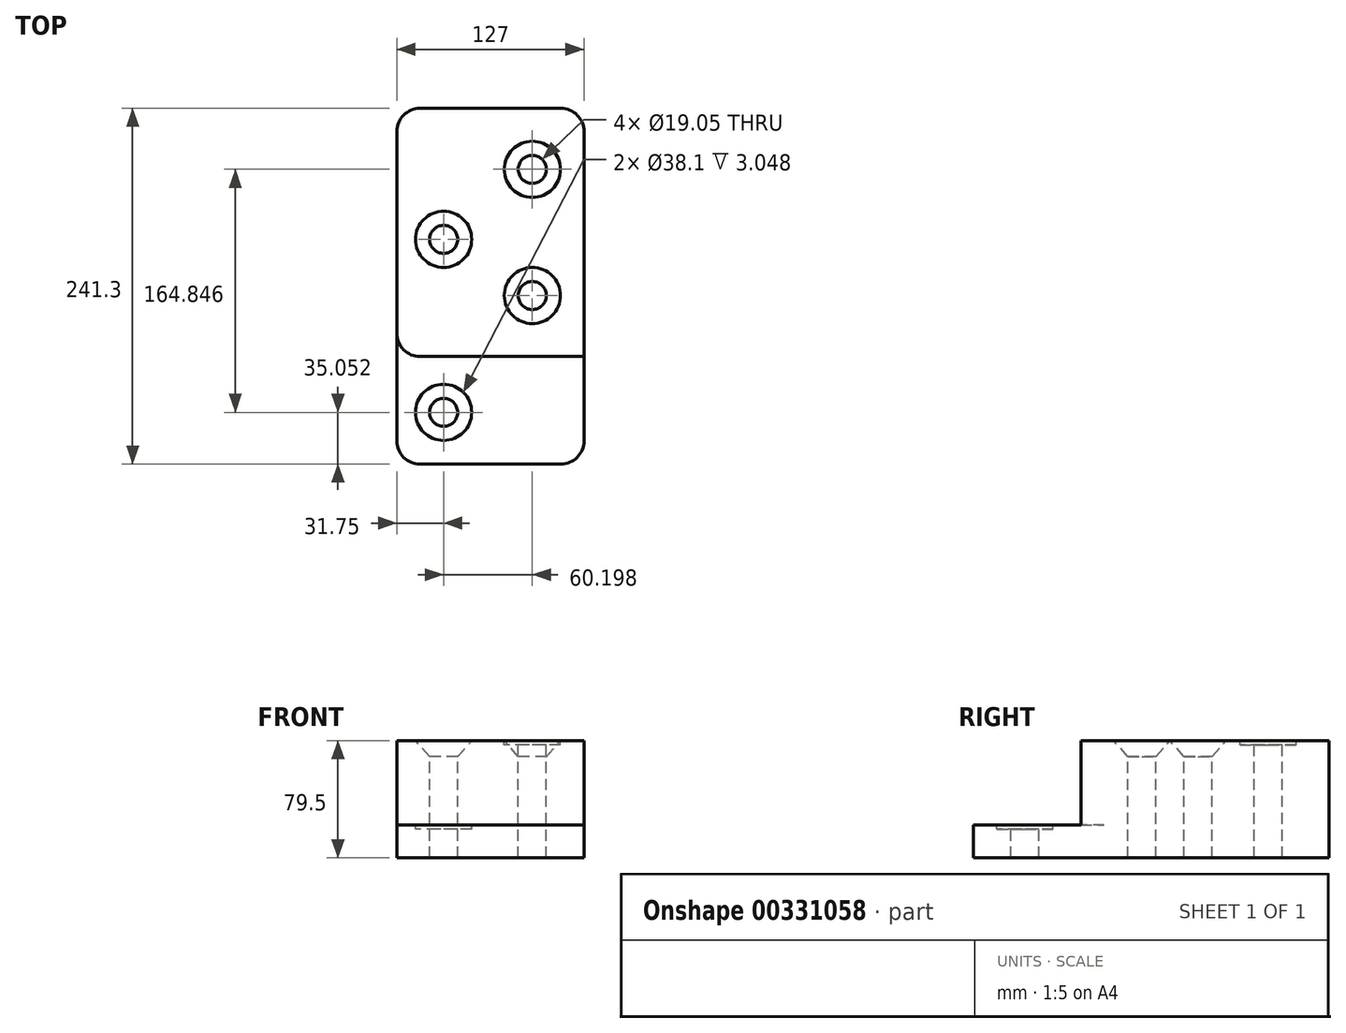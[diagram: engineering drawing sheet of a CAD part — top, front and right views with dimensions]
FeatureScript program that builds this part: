
annotation { "Feature Type Name" : "Feature", "Feature Type Description" : "" }
export const myFeature = defineFeature(function(context is Context, id is Id, definition is map)
    precondition{}
    {
        {
            var Q0;
            Q0=qCreatedBy(makeId("Front.planeOp"),FACE);
            var sketch = newSketch(context, id + "F0", { "sketchPlane" : qUnion([Q0])});
            skLineSegment(sketch, "E0", {"start": v(-63.5, 0) * mm, "end": v(63.5, 0) * mm});
            skLineSegment(sketch, "E1", {"start": v(63.5, 0) * mm, "end": v(63.5, 79.5) * mm});
            skLineSegment(sketch, "E2", {"start": v(63.5, 79.5) * mm, "end": v(-63.5, 79.5) * mm});
            skLineSegment(sketch, "E3", {"start": v(-63.5, 79.5) * mm, "end": v(-63.5, 0) * mm});
            skSolve(sketch);
        }
        {
            var Q0;
            Q0 = qSketchRegion(id + "F0", true);
            extrude(context, id + "F1", {"entities" : qUnion([Q0]), "oppositeDirection" : true, "depth" : 241.3 * mm});
        }
        {
            var Q0;
            Q0=makeQuery(id+"F1.opExtrude","SWEPT_FACE",FACE,{"disambiguationData":[OSD([sQuery(id+"F0.wireOp",EDGE,"E1")])]});
            var sketch = newSketch(context, id + "F2", { "sketchPlane" : qUnion([Q0])});
            skLineSegment(sketch, "E4.0", {"start": v(72.9, 79.5) * mm, "end": v(0, 79.5) * mm});
            skLineSegment(sketch, "E5.0", {"start": v(0, 22.35) * mm, "end": v(0, 79.5) * mm});
            skLineSegment(sketch, "E6", {"start": v(0, 22.35) * mm, "end": v(72.9, 22.35) * mm});
            skLineSegment(sketch, "E7", {"start": v(72.9, 22.35) * mm, "end": v(72.9, 79.5) * mm});
            skPoint(sketch, "E8.orphan", {"position": v(241.3, 79.5) * mm});
            skPoint(sketch, "E9.orphan", {"position": v(0, 0) * mm});
            skLineSegment(sketch, "E10.0", {"start": v(241.3, 0) * mm, "end": v(0, 0) * mm});
            skSolve(sketch);
        }
        {
            var Q0;
            Q0 = qSketchRegion(id + "F2", true);
            extrude(context, id + "F3", {"entities" : qUnion([Q0]), "operationType" : NewBodyOperationType.REMOVE, "endBound" : BoundingType.THROUGH_ALL, "oppositeDirection" : true, "depth" : 25.4 * mm});
        }
        {
            var Q0;
            Q0=makeQuery(id+"F3.boolean.opBoolean","COPY",FACE,{"derivedFrom":makeQuery(id+"F3.opExtrude","SWEPT_FACE",FACE,{"disambiguationData":[OSD([sQuery(id+"F2.wireOp",EDGE,"E6")])]})});
            var sketch = newSketch(context, id + "F4", { "sketchPlane" : qUnion([Q0])});
            skPoint(sketch, "E11", {"position": v(-31.75, 35.05) * mm});
            skLineSegment(sketch, "E12.0", {"start": v(63.5, 0) * mm, "end": v(63.5, 72.9) * mm});
            skLineSegment(sketch, "E13.0", {"start": v(-63.5, 0) * mm, "end": v(63.5, 0) * mm});
            skPoint(sketch, "E14", {"position": v(28.45, 199.9) * mm});
            skLineSegment(sketch, "E15.0", {"start": v(63.5, 241.3) * mm, "end": v(63.5, 72.9) * mm});
            skLineSegment(sketch, "E16.0", {"start": v(63.5, 241.3) * mm, "end": v(-63.5, 241.3) * mm});
            skLineSegment(sketch, "E17.0", {"start": v(-63.5, 72.9) * mm, "end": v(63.5, 72.9) * mm});
            skSolve(sketch);
        }
        {
            var Q0;
            Q0=makeQuery(id+"F1.opExtrude","SWEPT_FACE",FACE,{"disambiguationData":[OSD([sQuery(id+"F0.wireOp",EDGE,"E2")])]});
            var sketch = newSketch(context, id + "F5", { "sketchPlane" : qUnion([Q0])});
            skPoint(sketch, "E18", {"position": v(-31.75, 152.4) * mm});
            skPoint(sketch, "E19", {"position": v(28.45, 206.25) * mm});
            skPoint(sketch, "E20", {"position": v(28.45, 114.3) * mm});
            skLineSegment(sketch, "E21.0", {"start": v(-63.5, 241.3) * mm, "end": v(-63.5, 72.9) * mm});
            skPoint(sketch, "E22.0", {"position": v(0, 72.9) * mm});
            skLineSegment(sketch, "E23.0", {"start": v(-63.5, 72.9) * mm, "end": v(63.5, 72.9) * mm});
            skLineSegment(sketch, "E24.0.0", {"start": v(63.5, 72.9) * mm, "end": v(63.5, 0) * mm});
            skLineSegment(sketch, "E24.0.2", {"start": v(63.5, 72.9) * mm, "end": v(63.5, 241.3) * mm});
            skLineSegment(sketch, "E24.0.4", {"start": v(63.5, 241.3) * mm, "end": v(63.5, 72.9) * mm});
            skLineSegment(sketch, "E25.0", {"start": v(63.5, 241.3) * mm, "end": v(-63.5, 241.3) * mm});
            skPoint(sketch, "E26.orphan", {"position": v(63.5, 0) * mm});
            skSolve(sketch);
        }
        {
            var Q0;
            Q0=sQuery(id+"F5.wireOp",VERTEX,"E18");
            var Q1;
            Q1=sQuery(id+"F5.wireOp",VERTEX,"E20");
            var Q2;
            Q2=makeQuery(id+"F1.opExtrude","SWEPT_BODY",BODY,{"disambiguationData":[OSD([sQuery(id+"F0.wireOp",EDGE,"E0"),sQuery(id+"F0.wireOp",EDGE,"E1"),sQuery(id+"F0.wireOp",EDGE,"E2"),sQuery(id+"F0.wireOp",EDGE,"E3")])]});
            hole(context, id + "F6", {"style" : HoleStyle.C_SINK, "endStyle" : HoleEndStyle.THROUGH, "holeDiameter" : 19.05 * mm, "cSinkDiameter" : 38.1 * mm, "cSinkAngle" : 82 * degree, "tappedDepth" : 12.7 * mm, "tapClearance" : 3, "locations" : qUnion([Q0, Q1]), "scope" : qUnion([Q2])});
        }
        {
            var Q0;
            Q0=sQuery(id+"F4.wireOp",VERTEX,"E11");
            var Q1;
            Q1=makeQuery(id+"F1.opExtrude","SWEPT_BODY",BODY,{"disambiguationData":[OSD([sQuery(id+"F0.wireOp",EDGE,"E0"),sQuery(id+"F0.wireOp",EDGE,"E1"),sQuery(id+"F0.wireOp",EDGE,"E2"),sQuery(id+"F0.wireOp",EDGE,"E3")])]});
            hole(context, id + "F7", {"style" : HoleStyle.C_BORE, "endStyle" : HoleEndStyle.THROUGH, "holeDiameter" : 19.05 * mm, "cBoreDiameter" : 38.1 * mm, "cBoreDepth" : 3.05 * mm, "tappedDepth" : 12.7 * mm, "tapClearance" : 3, "locations" : qUnion([Q0]), "scope" : qUnion([Q1])});
        }
        {
            var Q0;
            Q0=makeQuery(id+"F1.opExtrude","SWEPT_FACE",FACE,{"disambiguationData":[OSD([sQuery(id+"F0.wireOp",EDGE,"E2")])]});
            var sketch = newSketch(context, id + "F8", { "sketchPlane" : qUnion([Q0])});
            skPoint(sketch, "E27", {"position": v(28.45, 199.9) * mm});
            skLineSegment(sketch, "E28.0", {"start": v(63.5, 241.3) * mm, "end": v(-63.5, 241.3) * mm});
            skLineSegment(sketch, "E29.0", {"start": v(63.5, 241.3) * mm, "end": v(63.5, 72.9) * mm});
            skSolve(sketch);
        }
        {
            var Q0;
            Q0=sQuery(id+"F8.wireOp",VERTEX,"E27");
            var Q1;
            Q1=makeQuery(id+"F1.opExtrude","SWEPT_BODY",BODY,{"disambiguationData":[OSD([sQuery(id+"F0.wireOp",EDGE,"E0"),sQuery(id+"F0.wireOp",EDGE,"E1"),sQuery(id+"F0.wireOp",EDGE,"E2"),sQuery(id+"F0.wireOp",EDGE,"E3")])]});
            hole(context, id + "F9", {"style" : HoleStyle.C_BORE, "endStyle" : HoleEndStyle.THROUGH, "holeDiameter" : 19.05 * mm, "cBoreDiameter" : 38.1 * mm, "cBoreDepth" : 3.05 * mm, "tappedDepth" : 12.7 * mm, "tapClearance" : 3, "locations" : qUnion([Q0]), "scope" : qUnion([Q1])});
        }
        {
            var Q0;
            Q0=makeQuery(id+"F3.boolean.opBoolean","COPY",EDGE,{"derivedFrom":makeQuery(id+"F3.opExtrude","CAP_EDGE",EDGE,{"disambiguationData":[OSD([sQuery(id+"F2.wireOp",EDGE,"E7")])],"isStart":true})});
            var Q1;
            Q1=makeQuery(id+"F3.boolean.opBoolean","INTERSECT",EDGE,{"derivedFrom":[makeQuery(id+"F1.opExtrude","SWEPT_FACE",FACE,{"disambiguationData":[OSD([sQuery(id+"F0.wireOp",EDGE,"E3")])]}),makeQuery(id+"F3.opExtrude","SWEPT_FACE",FACE,{"disambiguationData":[OSD([sQuery(id+"F2.wireOp",EDGE,"E7")])]})]});
            var Q2;
            Q2=makeQuery(id+"F1.opExtrude","CAP_EDGE",EDGE,{"disambiguationData":[OSD([sQuery(id+"F0.wireOp",EDGE,"E3")])],"isStart":true});
            var Q3;
            Q3=makeQuery(id+"F1.opExtrude","CAP_EDGE",EDGE,{"disambiguationData":[OSD([sQuery(id+"F0.wireOp",EDGE,"E1")])],"isStart":true});
            var Q4;
            Q4=makeQuery(id+"F1.opExtrude","CAP_EDGE",EDGE,{"disambiguationData":[OSD([sQuery(id+"F0.wireOp",EDGE,"E1")])],"isStart":false});
            var Q5;
            Q5=makeQuery(id+"F1.opExtrude","CAP_EDGE",EDGE,{"disambiguationData":[OSD([sQuery(id+"F0.wireOp",EDGE,"E3")])],"isStart":false});
            fillet(context, id + "F10", {"entities" : qUnion([Q0, Q1, Q2, Q3, Q4, Q5]), "radius" : 15.75 * mm, "tangentPropagation" : true, "allowEdgeOverflow" : false});
        }
    });
